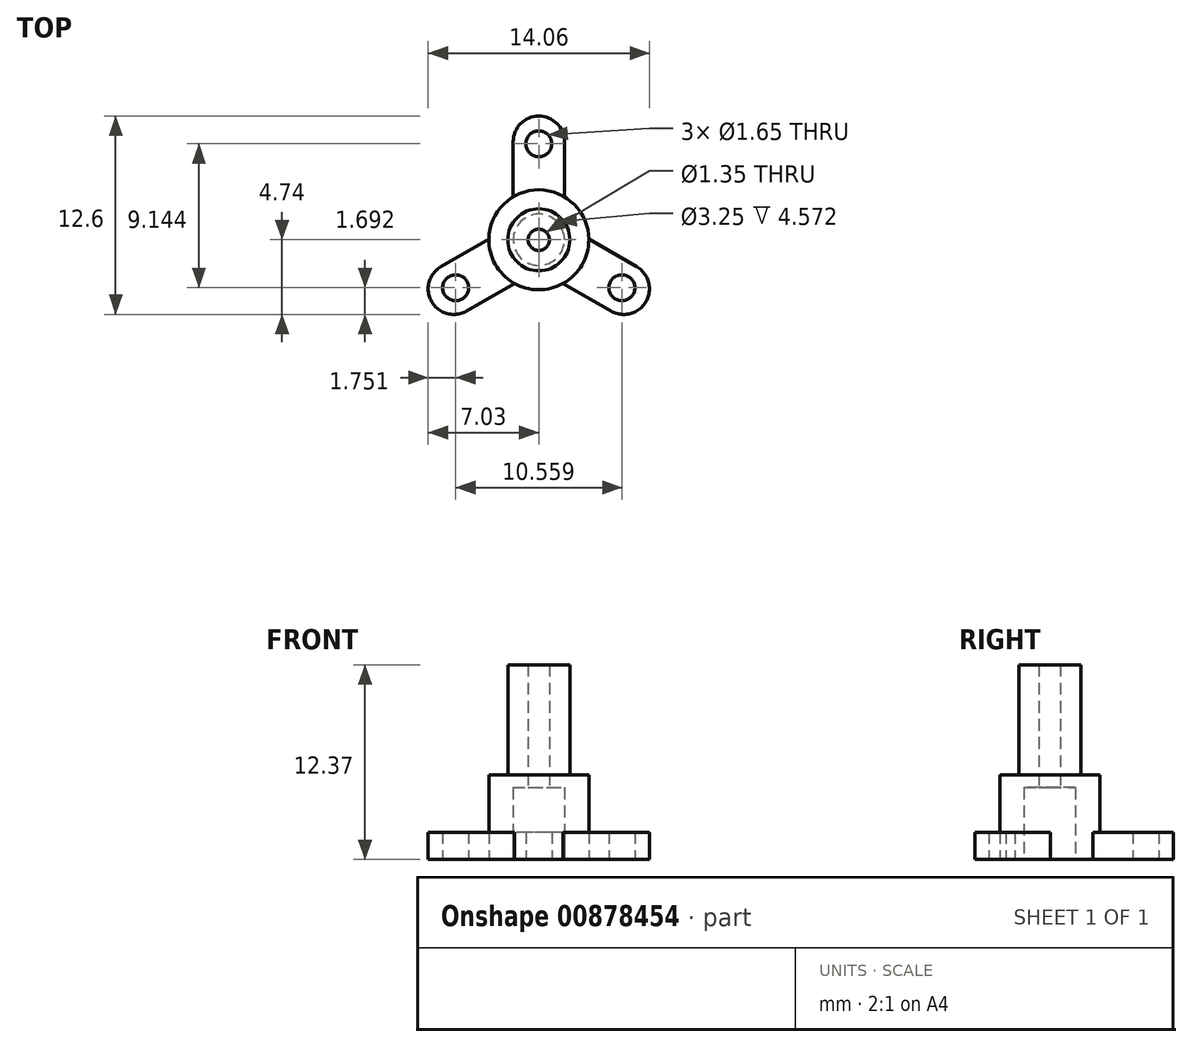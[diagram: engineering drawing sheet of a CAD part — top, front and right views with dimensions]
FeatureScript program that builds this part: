
annotation { "Feature Type Name" : "Feature", "Feature Type Description" : "" }
export const myFeature = defineFeature(function(context is Context, id is Id, definition is map)
    precondition{}
    {
        {
            var Q0;
            Q0=qCreatedBy(makeId("Top.planeOp"),FACE);
            var sketch = newSketch(context, id + "F0", { "sketchPlane" : qUnion([Q0])});
            skLineSegment(sketch, "E0", {"start": v(0, 0) * mm, "end": v(0, 61.16) * mm, "construction": true});
            skLineSegment(sketch, "E1", {"start": v(0, 0) * mm, "end": v(-49.57, -28.62) * mm, "construction": true});
            skLineSegment(sketch, "E2", {"start": v(0, 0) * mm, "end": v(45.9, -26.5) * mm, "construction": true});
            skLineSegment(sketch, "E3.0", {"start": v(1.55, -2.77) * mm, "end": v(4.59, -4.53) * mm});
            skLineSegment(sketch, "E4.0", {"start": v(3.17, 0.04) * mm, "end": v(6.21, -1.71) * mm});
            skArc(sketch, "E5", {"start": v(-1.63, 2.73) * mm, "mid": v(-2.75, 1.59) * mm, "end": v(-3.17, 0.04) * mm});
            skLineSegment(sketch, "E6.trimOffspring", {"start": v(-1.63, 2.73) * mm, "end": v(-1.63, 6.24) * mm});
            skLineSegment(sketch, "E7.trimOffspring", {"start": v(-3.17, 0.04) * mm, "end": v(-6.21, -1.71) * mm});
            skLineSegment(sketch, "E8.trimOffspring", {"start": v(-1.55, -2.77) * mm, "end": v(-4.59, -4.53) * mm});
            skLineSegment(sketch, "E9.trimOffspring", {"start": v(1.63, 2.73) * mm, "end": v(1.63, 6.24) * mm});
            skCircle(sketch, "E10", {"center": v(0, 6.1) * mm, "radius": 0.83 * mm});
            skCircle(sketch, "E11", {"center": v(-5.28, -3.05) * mm, "radius": 0.83 * mm});
            skCircle(sketch, "E12", {"center": v(5.28, -3.05) * mm, "radius": 0.83 * mm});
            skLineSegment(sketch, "E13", {"start": v(0, 7.86) * mm, "end": v(0, 7.86) * mm});
            skLineSegment(sketch, "E14", {"start": v(-6.8, -3.93) * mm, "end": v(-6.8, -3.93) * mm});
            skLineSegment(sketch, "E15", {"start": v(6.8, -3.93) * mm, "end": v(6.8, -3.93) * mm});
            skArc(sketch, "E16.filletArc", {"start": v(1.63, 6.24) * mm, "mid": v(1.15, 7.39) * mm, "end": v(0, 7.86) * mm});
            skArc(sketch, "E17.filletArc", {"start": v(0, 7.86) * mm, "mid": v(-1.15, 7.39) * mm, "end": v(-1.63, 6.24) * mm});
            skArc(sketch, "E18.filletArc", {"start": v(-6.21, -1.71) * mm, "mid": v(-6.97, -2.7) * mm, "end": v(-6.8, -3.93) * mm});
            skArc(sketch, "E19.filletArc", {"start": v(-6.8, -3.93) * mm, "mid": v(-5.82, -4.69) * mm, "end": v(-4.59, -4.53) * mm});
            skArc(sketch, "E20.filletArc", {"start": v(4.59, -4.53) * mm, "mid": v(5.82, -4.69) * mm, "end": v(6.8, -3.93) * mm});
            skArc(sketch, "E21.filletArc", {"start": v(6.8, -3.93) * mm, "mid": v(6.97, -2.7) * mm, "end": v(6.21, -1.71) * mm});
            skArc(sketch, "E22.trimOffspring", {"start": v(-1.55, -2.77) * mm, "mid": v(0, -3.17) * mm, "end": v(1.55, -2.77) * mm});
            skArc(sketch, "E23.trimOffspring", {"start": v(3.17, 0.04) * mm, "mid": v(2.75, 1.59) * mm, "end": v(1.63, 2.73) * mm});
            skSolve(sketch);
        }
        {
            var Q0;
            Q0 = qSketchRegion(id + "F0", true);
            extrude(context, id + "F1", {"entities" : qUnion([Q0]), "depth" : 1.73 * mm, "offsetDistance" : 25.4 * mm});
        }
        {
            var Q0;
            Q0=makeQuery(id+"F1.opExtrude","CAP_FACE",FACE,{"disambiguationData":[OSD([sQuery(id+"F0.wireOp",EDGE,"E3.0"),sQuery(id+"F0.wireOp",EDGE,"E4.0"),sQuery(id+"F0.wireOp",EDGE,"E5"),sQuery(id+"F0.wireOp",EDGE,"E6.trimOffspring"),sQuery(id+"F0.wireOp",EDGE,"E7.trimOffspring"),sQuery(id+"F0.wireOp",EDGE,"E8.trimOffspring"),sQuery(id+"F0.wireOp",EDGE,"E9.trimOffspring"),sQuery(id+"F0.wireOp",EDGE,"E10"),sQuery(id+"F0.wireOp",EDGE,"E11"),sQuery(id+"F0.wireOp",EDGE,"E12"),sQuery(id+"F0.wireOp",EDGE,"E16.filletArc"),sQuery(id+"F0.wireOp",EDGE,"E17.filletArc"),sQuery(id+"F0.wireOp",EDGE,"E18.filletArc"),sQuery(id+"F0.wireOp",EDGE,"E19.filletArc"),sQuery(id+"F0.wireOp",EDGE,"E20.filletArc"),sQuery(id+"F0.wireOp",EDGE,"E21.filletArc"),sQuery(id+"F0.wireOp",EDGE,"E22.trimOffspring"),sQuery(id+"F0.wireOp",EDGE,"E23.trimOffspring")])],"isStart":false});
            var sketch = newSketch(context, id + "F2", { "sketchPlane" : qUnion([Q0])});
            skCircle(sketch, "E24", {"center": v(0, 0) * mm, "radius": 3.18 * mm});
            skSolve(sketch);
        }
        {
            var Q0;
            Q0 = qSketchRegion(id + "F2", true);
            extrude(context, id + "F3", {"entities" : qUnion([Q0]), "operationType" : NewBodyOperationType.ADD, "depth" : 3.66 * mm, "offsetDistance" : 25.4 * mm});
        }
        {
            var Q0;
            Q0=makeQuery(id+"F3.opExtrude","CAP_FACE",FACE,{"disambiguationData":[OSD([sQuery(id+"F2.wireOp",EDGE,"E24")])],"isStart":false});
            var sketch = newSketch(context, id + "F4", { "sketchPlane" : qUnion([Q0])});
            skCircle(sketch, "E25", {"center": v(0, 0) * mm, "radius": 1.97 * mm});
            skSolve(sketch);
        }
        {
            var Q0;
            Q0 = qSketchRegion(id + "F4", true);
            extrude(context, id + "F5", {"entities" : qUnion([Q0]), "operationType" : NewBodyOperationType.ADD, "depth" : 7 * mm, "offsetDistance" : 25.4 * mm});
        }
        {
            var Q0;
            Q0=qCreatedBy(makeId("Top.planeOp"),FACE);
            var sketch = newSketch(context, id + "F6", { "sketchPlane" : qUnion([Q0])});
            skCircle(sketch, "E26", {"center": v(0, 0) * mm, "radius": 0.67 * mm});
            skSolve(sketch);
        }
        {
            var Q0;
            Q0 = qSketchRegion(id + "F6", true);
            extrude(context, id + "F7", {"entities" : qUnion([Q0]), "operationType" : NewBodyOperationType.REMOVE, "endBound" : BoundingType.THROUGH_ALL, "depth" : 25.4 * mm, "offsetDistance" : 25.4 * mm});
        }
        {
            var Q0;
            Q0=makeQuery(id+"F1.opExtrude","CAP_FACE",FACE,{"disambiguationData":[OSD([sQuery(id+"F0.wireOp",EDGE,"E3.0"),sQuery(id+"F0.wireOp",EDGE,"E4.0"),sQuery(id+"F0.wireOp",EDGE,"E5"),sQuery(id+"F0.wireOp",EDGE,"E6.trimOffspring"),sQuery(id+"F0.wireOp",EDGE,"E7.trimOffspring"),sQuery(id+"F0.wireOp",EDGE,"E8.trimOffspring"),sQuery(id+"F0.wireOp",EDGE,"E9.trimOffspring"),sQuery(id+"F0.wireOp",EDGE,"E10"),sQuery(id+"F0.wireOp",EDGE,"E11"),sQuery(id+"F0.wireOp",EDGE,"E12"),sQuery(id+"F0.wireOp",EDGE,"E16.filletArc"),sQuery(id+"F0.wireOp",EDGE,"E17.filletArc"),sQuery(id+"F0.wireOp",EDGE,"E18.filletArc"),sQuery(id+"F0.wireOp",EDGE,"E19.filletArc"),sQuery(id+"F0.wireOp",EDGE,"E20.filletArc"),sQuery(id+"F0.wireOp",EDGE,"E21.filletArc"),sQuery(id+"F0.wireOp",EDGE,"E22.trimOffspring"),sQuery(id+"F0.wireOp",EDGE,"E23.trimOffspring")])],"isStart":true});
            var sketch = newSketch(context, id + "F8", { "sketchPlane" : qUnion([Q0])});
            skCircle(sketch, "E27", {"center": v(0, 0) * mm, "radius": 1.63 * mm});
            skSolve(sketch);
        }
        {
            var Q0;
            Q0 = qSketchRegion(id + "F8", true);
            extrude(context, id + "F9", {"entities" : qUnion([Q0]), "operationType" : NewBodyOperationType.REMOVE, "oppositeDirection" : true, "depth" : 4.57 * mm, "offsetDistance" : 25.4 * mm});
        }
    });
